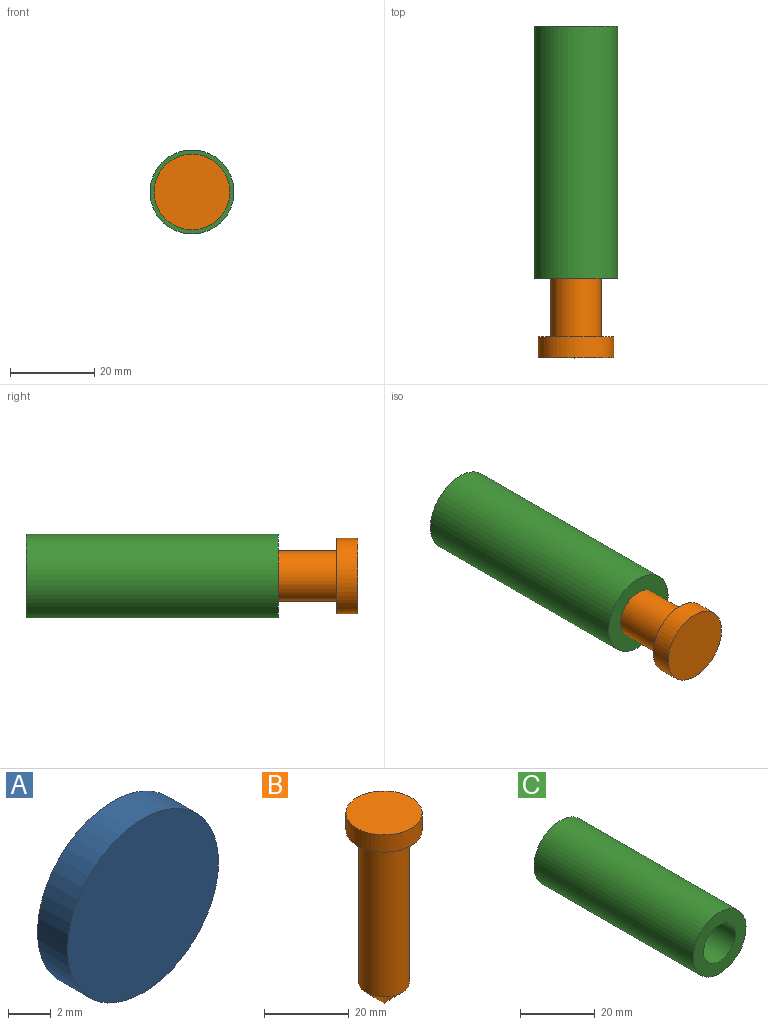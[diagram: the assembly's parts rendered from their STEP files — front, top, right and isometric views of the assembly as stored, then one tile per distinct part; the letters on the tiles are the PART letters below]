
ASSEMBLY  parts=3 mates=2
PART A: 3 faces, bbox 10x2x10 mm
  f0: cylinder r=5mm len=10mm, axis (0,1,0), area 62.8mm2, adj f1,f2
  f1: plane 10x10mm, normal (0,-1,0), area 78.5mm2, adj f0
  f2: plane 10x10mm, normal (0,1,0), area 78.5mm2, adj f0
PART B: 5 faces, bbox 18x18x55 mm
  f0: cone r=0mm half-angle=45deg, axis (0,0,1), area 159.9mm2, adj f1
  f1: cylinder r=6mm len=44mm, axis (0,0,1), area 1658.8mm2, adj f0,f2
  f2: plane 18x18mm, normal (0,0,-1), area 141.4mm2, adj f1,f3
  f3: cylinder r=9mm len=18mm, axis (0,0,1), area 282.7mm2, adj f2,f4
  f4: plane 18x18mm, normal (0,0,1), area 254.5mm2, adj f3
PART C: 8 faces, bbox 20x60x20 mm
  f0: cylinder r=10mm len=60mm, axis (0,1,0), area 3769.9mm2, adj f1,f2
  f1: plane 20x20mm, normal (0,-1,0), area 201.1mm2, adj f0,f3
  f2: plane 20x20mm, normal (0,1,0), area 301.6mm2, adj f0,f7
  f3: cylinder r=6mm len=45mm, axis (0,-1,0), area 1696.5mm2, adj f1,f4
  f4: plane 12x12mm, normal (0,-1,0), area 34.6mm2, adj f3,f5
  f5: cylinder r=5mm len=10mm, axis (0,-1,0), area 15.7mm2, adj f4,f6
  f6: plane 10x10mm, normal (0,-1,0), area 66mm2, adj f5,f7
  f7: cylinder r=2mm len=14.5mm, axis (0,-1,0), area 182.2mm2, adj f2,f6
PLACE A rot(axis=(-1,0,0),180deg) t=(-0.8,-4.17,2.64)mm
PLACE B rot(axis=(1,0,0),90deg) t=(-0.8,-11.67,2.64)mm
PLACE C rot(axis=(0,1,0),0deg) t=(-0.8,12.33,2.64)mm
MATE cylindrical A.f0 <-> C.f5  axis (0,1,0) through (-0.8,-2.17,2.64)mm
MATE pin_slot B.f0 <-> C.f3  axis (0,-1,0) through (-0.8,-17.67,2.64)mm
